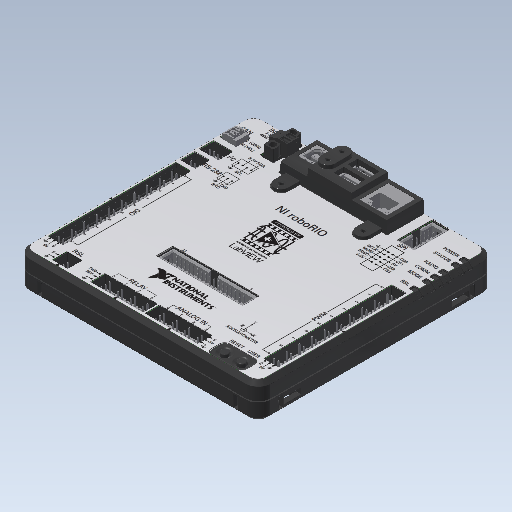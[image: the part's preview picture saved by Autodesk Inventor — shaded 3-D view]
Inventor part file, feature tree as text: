
AUTODESK INVENTOR PART (.ipt)
format: ipt  version: 2020 (Build 240168000, 168)  size: 41,439,744 bytes
history: native  units: in
note: dims shown in document units (in); Inventor stores cm internally (conversion verified against a paired STEP export)
features: imported_body x15, other x4, sketch x1
ambient origin geometry x8: Origin, YZ Plane, XZ Plane, XY Plane, X Axis, Y Axis, Z Axis, Center Point
bodies: Solid1 (feature_tree), Solid2 (feature_tree), Solid3 (feature_tree), Solid4 (feature_tree), Solid5 (feature_tree), Solid6 (feature_tree), Solid7 (feature_tree), Solid8 (feature_tree), Solid9 (feature_tree), Solid10 (feature_tree), Solid11 (feature_tree), Solid12 (feature_tree), Solid13 (feature_tree), Solid14 (feature_tree), Solid15 (feature_tree), Solid16 (feature_tree)
feature tree (20):
  other  "cd_roborio1"
  other  "Decal1"
  imported_body  "Base1"
  imported_body  "Base2"
  imported_body  "Base3"
  imported_body  "Base4"
  imported_body  "Base5"
  other  "roboRIO CASE"
  imported_body  "Base7"
  imported_body  "Base8"
  imported_body  "Base9"
  imported_body  "Base10"
  imported_body  "Base11"
  imported_body  "Base12"
  imported_body  "Base13"
  imported_body  "Base14"
  imported_body  "Base15"
  imported_body  "Base16"
  sketch  "Sketch1"
  other  "Image1"
